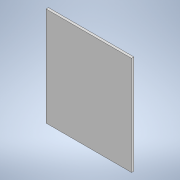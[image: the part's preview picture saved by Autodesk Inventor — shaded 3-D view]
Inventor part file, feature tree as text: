
AUTODESK INVENTOR PART (.ipt)
format: ipt  version: 2021 (Build 250183000, 183)  size: 91,136 bytes
history: native  units: mm
features: extrude x1, sketch x1
ambient origin geometry x8: Origin, YZ Plane, XZ Plane, XY Plane, X Axis, Y Axis, Z Axis, Center Point
bodies: Solid1 (feature_tree)
feature tree (2):
  extrude  "Extrusion1"  Depth=81.8mm
  sketch  "Sketch1"  dims[d0=70.8mm d1=81.8mm d2=2.0mm d3=0.0mm d8=0.5mm d9=0.872665mm d10=0.5mm d11=0.872665mm]
